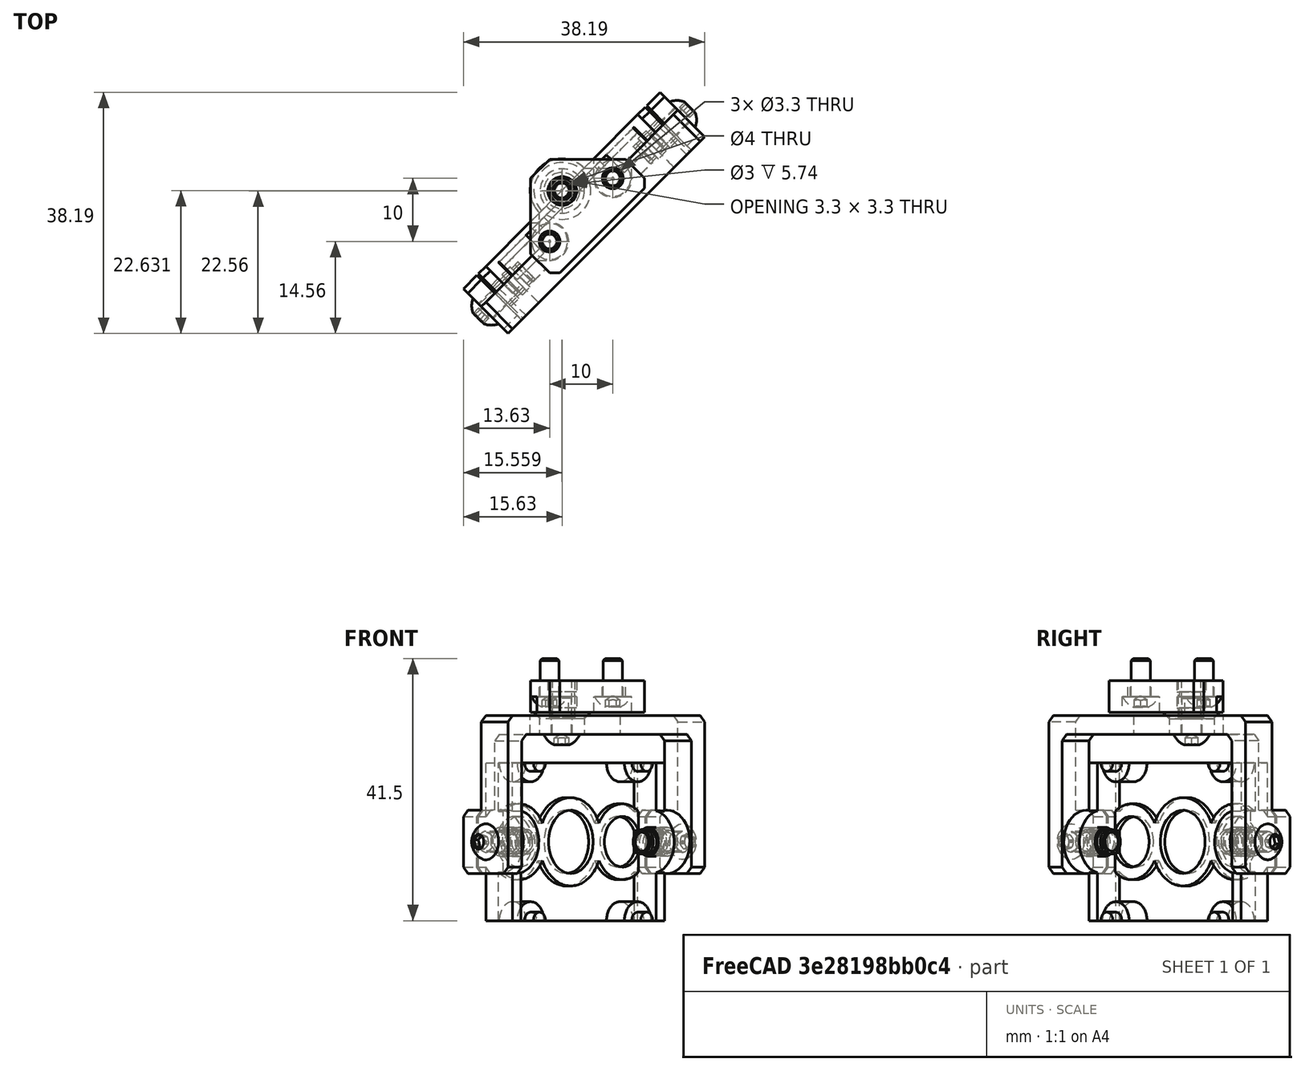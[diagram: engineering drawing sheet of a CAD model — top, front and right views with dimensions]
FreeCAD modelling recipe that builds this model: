
FCSTD DOCUMENT  (FreeCAD 0.19R24291 (Git))
Label: addon-camera-assembly
License: All rights reserved
LicenseURL: http://en.wikipedia.org/wiki/All_rights_reserved
objects: Part::FeaturePython×8, Part::Feature×3, PartDesign::CoordinateSystem×1, App::Part×1
note: 12 computed .brp shape members not serialized (recipe doc carries the construction recipe); baked Part::Feature solids carry a one-line shape summary decoded from their .brp

FEATURE [Part::Feature] Chamfer004001001  label="camera-arm"
  shape: bbox 38.18 x 38.18 x 25 mm, 33 faces (baked)
FEATURE [Part::FeaturePython] HeatSet003  label="M3x3-HeatSet003"  # WARN: FeaturePython — macro-defined, semantics opaque (R4)
  Placement = pos=(-16.7231,-9.65201,-20.5) rot=(0.707107,-0.707107,0;1.5708rad)
  baseObject = -> Cut003002001 [Edge170]
  diameter = 2
  invert = true
  offset = 0
FEATURE [Part::FeaturePython] HeatSet004  label="M3x3-HeatSet004"  # WARN: FeaturePython — macro-defined, semantics opaque (R4)
  Placement = pos=(9.65201,16.7231,-20.5) rot=(-0.707107,0.707107,0;1.5708rad)
  baseObject = -> Cut003002001 [Edge150]
  diameter = 2
  invert = false
  offset = 0
FEATURE [Part::FeaturePython] Screw006  label="M3x6-Screw013"  # Fasteners workbench fastener (typed FeaturePython)
  Placement = pos=(-19.0919,-12.0208,-20.5) rot=(0.707107,-0.707107,0;1.5708rad)
  baseObject = -> Chamfer004001001 [Edge88]
  diameter = 1
  invert = false
  length = 0
  lengthCustom = 6
  matchOuter = true
  offset = 0
  thread = false
  type = 40
FEATURE [Part::FeaturePython] Screw007  label="M3x6-Screw016"  # Fasteners workbench fastener (typed FeaturePython)
  Placement = pos=(-7.07107,7.07107,-3.5) rot=(1,0,0;3.14159rad)
  baseObject = -> Chamfer004001001 [Edge83]
  diameter = 1
  invert = true
  length = 0
  lengthCustom = 6
  matchOuter = true
  offset = 0
  thread = false
  type = 40
FEATURE [Part::FeaturePython] HeatSet002  label="M3x3-HeatSet002"  # WARN: FeaturePython — macro-defined, semantics opaque (R4)
  Placement = pos=(-7,7,5) rot=(0,0,1;0rad)
  baseObject = -> Cut002008023012009006003002007001 [Edge53]
  diameter = 2
  invert = false
  offset = 0
FEATURE [Part::FeaturePython] Screw004  label="M3x6-Screw011"  # Fasteners workbench fastener (typed FeaturePython)
  Placement = pos=(-9,-1,2.5) rot=(1,0,0;3.14159rad)
  baseObject = -> Cut002008023012009006003002007001 [Edge61]
  diameter = 1
  invert = true
  length = 0
  lengthCustom = 6
  matchOuter = true
  offset = 0
  thread = false
  type = 40
FEATURE [Part::Feature] Cut002008023012009006003002007001  label="camera-axis"
  shape: bbox 18 x 18 x 6 mm, 23 faces (baked)
FEATURE [Part::Feature] Cut003002001  label="camera-back-plate"
  shape: bbox 33.45 x 33.45 x 25 mm, 58 faces (baked)
FEATURE [PartDesign::CoordinateSystem] LCS_camera
  AttacherType = Attacher::AttachEngine3D
FEATURE [Part::FeaturePython] Screw005  label="M3x6-Screw012"  # Fasteners workbench fastener (typed FeaturePython)
  Placement = pos=(1,9,2.5) rot=(1,0,0;3.14159rad)
  baseObject = -> Cut002008023012009006003002007001 [Edge58]
  diameter = 1
  invert = true
  length = 0
  lengthCustom = 6
  matchOuter = true
  offset = 0
  thread = false
  type = 40
FEATURE [Part::FeaturePython] Screw008  label="M3x6-Screw017"  # Fasteners workbench fastener (typed FeaturePython)
  Placement = pos=(12.0208,19.0919,-20.5) rot=(-0.707107,0.707107,0;1.5708rad)
  baseObject = -> Chamfer004001001 [Edge96]
  diameter = 1
  invert = true
  length = 0
  lengthCustom = 6
  matchOuter = true
  offset = 0
  thread = false
  type = 40
FEATURE [App::Part] Part001  label="camera"
  Group = -> [Cut003002001,Cut002008023012009006003002007001,HeatSet002,HeatSet003,HeatSet004,Screw005,Screw004,Chamfer004001001,Screw008,Screw007,Screw006,LCS_camera]
  Origin = -> Origin001
